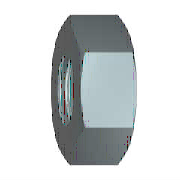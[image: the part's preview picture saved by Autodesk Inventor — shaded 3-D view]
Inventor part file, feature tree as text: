
AUTODESK INVENTOR PART (.ipt)
format: ipt  version: 2018 (Build 220112000, 112)  size: 161,792 bytes
history: native  units: mm (DEFAULTED — no unit token found)
features: sketch x3, chamfer x1, hole x1, other x1, plane x1
ambient origin geometry x7: Origin, YZ Plane, XZ Plane, X Axis, Y Axis, Z Axis, Center Point
bodies: Solid1 (feature_tree), Body (feature_tree)
feature tree (7):
  chamfer  "Chamfer1"  Angle=30.0deg  [1 undecoded]
  hole  "Thread"  [1 undecoded]
  other  "Work Axis1"
  plane  "Work Plane1"
  sketch  "Sketch1"  dims[d0=4.618802mm]
  sketch  "Sketch2"  dims[d1=1.6mm]
  sketch  "Sketch3"  dims[d2=0.0mm d3=30.0deg d4=30.0deg d5=3.2mm d6=3.2mm d7=90.0deg d25=1.567mm d26=6.0mm d27=4.0mm d28=2.0mm d29=14.3117mm d30=8.0mm d31=20.594885mm d8=0.216506mm d9=30.0deg d10=0.216506mm d11=30.0deg d13=0.0mm d14=0.0mm d39=0.0mm d40=0.216506mm d41=0.216506mm d42=0.0mm]
note: 2 required parameter values undecoded (feature->parameter linkage not recoverable at this tier; creation-order binding heuristic only, values carry confidence <= 0.55)
